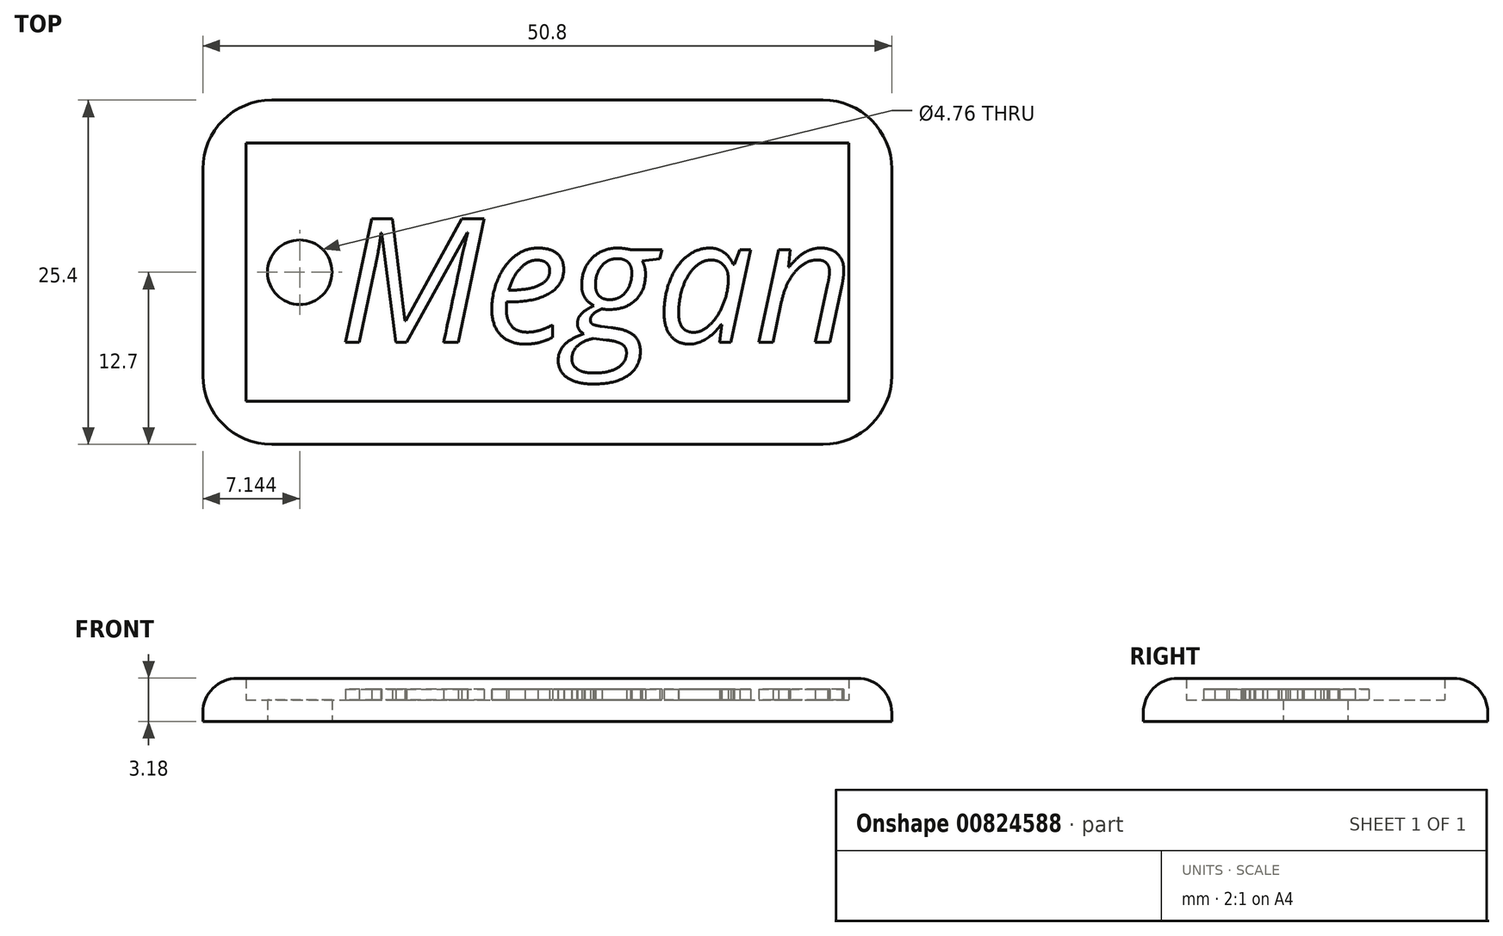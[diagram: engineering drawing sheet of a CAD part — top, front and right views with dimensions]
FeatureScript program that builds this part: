
annotation { "Feature Type Name" : "Feature", "Feature Type Description" : "" }
export const myFeature = defineFeature(function(context is Context, id is Id, definition is map)
    precondition{}
    {
        {
            var Q0;
            Q0=qCreatedBy(makeId("Top.planeOp"),FACE);
            var sketch = newSketch(context, id + "F0", { "sketchPlane" : qUnion([Q0])});
            skLineSegment(sketch, "E0.bottom", {"start": v(0, 0) * mm, "end": v(50.8, 0) * mm});
            skLineSegment(sketch, "E0.top", {"start": v(0, 25.4) * mm, "end": v(50.8, 25.4) * mm});
            skLineSegment(sketch, "E0.left", {"start": v(0, 0) * mm, "end": v(0, 25.4) * mm});
            skLineSegment(sketch, "E0.right", {"start": v(50.8, 0) * mm, "end": v(50.8, 25.4) * mm});
            skCircle(sketch, "E1", {"center": v(7.14, 12.7) * mm, "radius": 2.38 * mm});
            skPoint(sketch, "E1.centerSnap0", {"position": v(0, 12.7) * mm});
            skLineSegment(sketch, "E2.0", {"start": v(3.18, 22.23) * mm, "end": v(47.62, 22.23) * mm});
            skLineSegment(sketch, "E2.1", {"start": v(3.18, 3.18) * mm, "end": v(3.18, 22.22) * mm});
            skLineSegment(sketch, "E2.2", {"start": v(3.18, 3.18) * mm, "end": v(47.62, 3.18) * mm});
            skLineSegment(sketch, "E2.3", {"start": v(47.62, 3.18) * mm, "end": v(47.62, 22.23) * mm});
            skSolve(sketch);
        }
        {
            var Q0;
            Q0=makeQuery(id+"F0.imprint","IMPRINT",FACE,{"disambiguationData":[TD([[makeQuery(id+"F0.imprint","IMPRINT",EDGE,{"derivedFrom":sQuery(id+"F0.wireOp",EDGE,"E1")}),-1.0]])]});
            extrude(context, id + "F1", {"entities" : qUnion([Q0]), "depth" : 1.59 * mm, "offsetDistance" : 25.4 * mm});
        }
        {
            var Q0;
            Q0 = qSketchRegion(id + "F0", true);
            extrude(context, id + "F2", {"entities" : qUnion([Q0]), "operationType" : NewBodyOperationType.ADD, "depth" : 3.17 * mm, "offsetDistance" : 25.4 * mm});
        }
        {
            var Q0;
            Q0=makeQuery(id+"F2.opExtrude","SWEPT_EDGE",EDGE,{"disambiguationData":[OSD([sQuery(id+"F0.wireOp",EDGE,"E0.bottom"),sQuery(id+"F0.wireOp",EDGE,"E0.left")])]});
            var Q1;
            Q1=makeQuery(id+"F2.opExtrude","SWEPT_EDGE",EDGE,{"disambiguationData":[OSD([sQuery(id+"F0.wireOp",EDGE,"E0.bottom"),sQuery(id+"F0.wireOp",EDGE,"E0.right")])]});
            var Q2;
            Q2=makeQuery(id+"F2.opExtrude","SWEPT_EDGE",EDGE,{"disambiguationData":[OSD([sQuery(id+"F0.wireOp",EDGE,"E0.top"),sQuery(id+"F0.wireOp",EDGE,"E0.right")])]});
            var Q3;
            Q3=makeQuery(id+"F2.opExtrude","SWEPT_EDGE",EDGE,{"disambiguationData":[OSD([sQuery(id+"F0.wireOp",EDGE,"E0.top"),sQuery(id+"F0.wireOp",EDGE,"E0.left")])]});
            fillet(context, id + "F3", {"entities" : qUnion([Q0, Q1, Q2, Q3]), "radius" : 5.08 * mm, "tangentPropagation" : true, "allowEdgeOverflow" : false});
        }
        {
            var Q0;
            Q0=makeQuery(id+"F2.opExtrude","CAP_EDGE",EDGE,{"disambiguationData":[OSD([sQuery(id+"F0.wireOp",EDGE,"E0.bottom")])],"isStart":false});
            fillet(context, id + "F4", {"entities" : qUnion([Q0]), "radius" : 2.54 * mm, "tangentPropagation" : true, "allowEdgeOverflow" : false});
        }
        {
            var Q0;
            Q0=makeQuery(id+"F1.opExtrude","CAP_FACE",FACE,{"disambiguationData":[OSD([sQuery(id+"F0.wireOp",EDGE,"E1"),sQuery(id+"F0.wireOp",EDGE,"E2.0"),sQuery(id+"F0.wireOp",EDGE,"E2.1"),sQuery(id+"F0.wireOp",EDGE,"E2.2"),sQuery(id+"F0.wireOp",EDGE,"E2.3")])],"isStart":false});
            var sketch = newSketch(context, id + "F5", { "sketchPlane" : qUnion([Q0])});
            skText(sketch, "E3", { "text": "Megan", "fontName": "OpenSans-Italic.ttf"});
            const initialGuessF5  = {"E3": [0.01, 0.00752, 1, 0, 0.0092]};
            skSetInitialGuess(sketch, initialGuessF5);
            skSolve(sketch);
        }
        {
            var Q0;
            Q0 = qSketchRegion(id + "F5", true);
            extrude(context, id + "F6", {"entities" : qUnion([Q0]), "operationType" : NewBodyOperationType.ADD, "depth" : 0.8 * mm, "offsetDistance" : 25.4 * mm});
        }
    });
